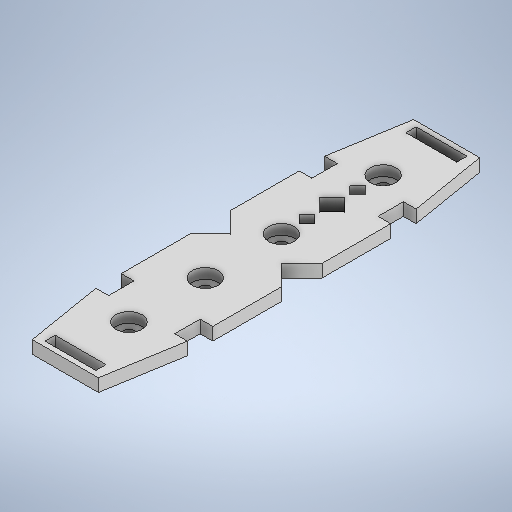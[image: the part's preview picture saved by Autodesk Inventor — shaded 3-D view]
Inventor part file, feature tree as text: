
AUTODESK INVENTOR PART (.ipt)
format: ipt  version: 2025.2 (Build 292293000, 293)  size: 329,728 bytes
history: native  units: mm
features: extrude x2, sketch x1
ambient origin geometry x8: Origin, YZ Plane, XZ Plane, XY Plane, X Axis, Y Axis, Z Axis, Center Point
bodies: Solid1 (feature_tree)
feature tree (3):
  sketch  "Sketch1"  dims[d2=10.2mm d3=25.0mm d4=10.2mm d5=30.0mm d6=10.2mm d7=30.0mm d8=10.2mm d9=40.0mm d10=25.0mm d12=5.0mm d13=10.0mm d15=10.0mm d17=5.0mm d19=5.0mm d20=5.0mm d21=0.0mm d22=4.5mm d23=4.5mm d24=4.5mm d25=4.5mm d26=1.0mm d27=0.0mm d38=3.0mm d39=2.0mm d41=2.0mm d42=4.0mm d44=2.0mm d45=3.0mm d46=4.0mm d50=8.0mm d51=8.0mm]
  extrude  "Extrusion1"  Depth=8.0mm
  extrude  "Extrusion2"  Depth=8.0mm
